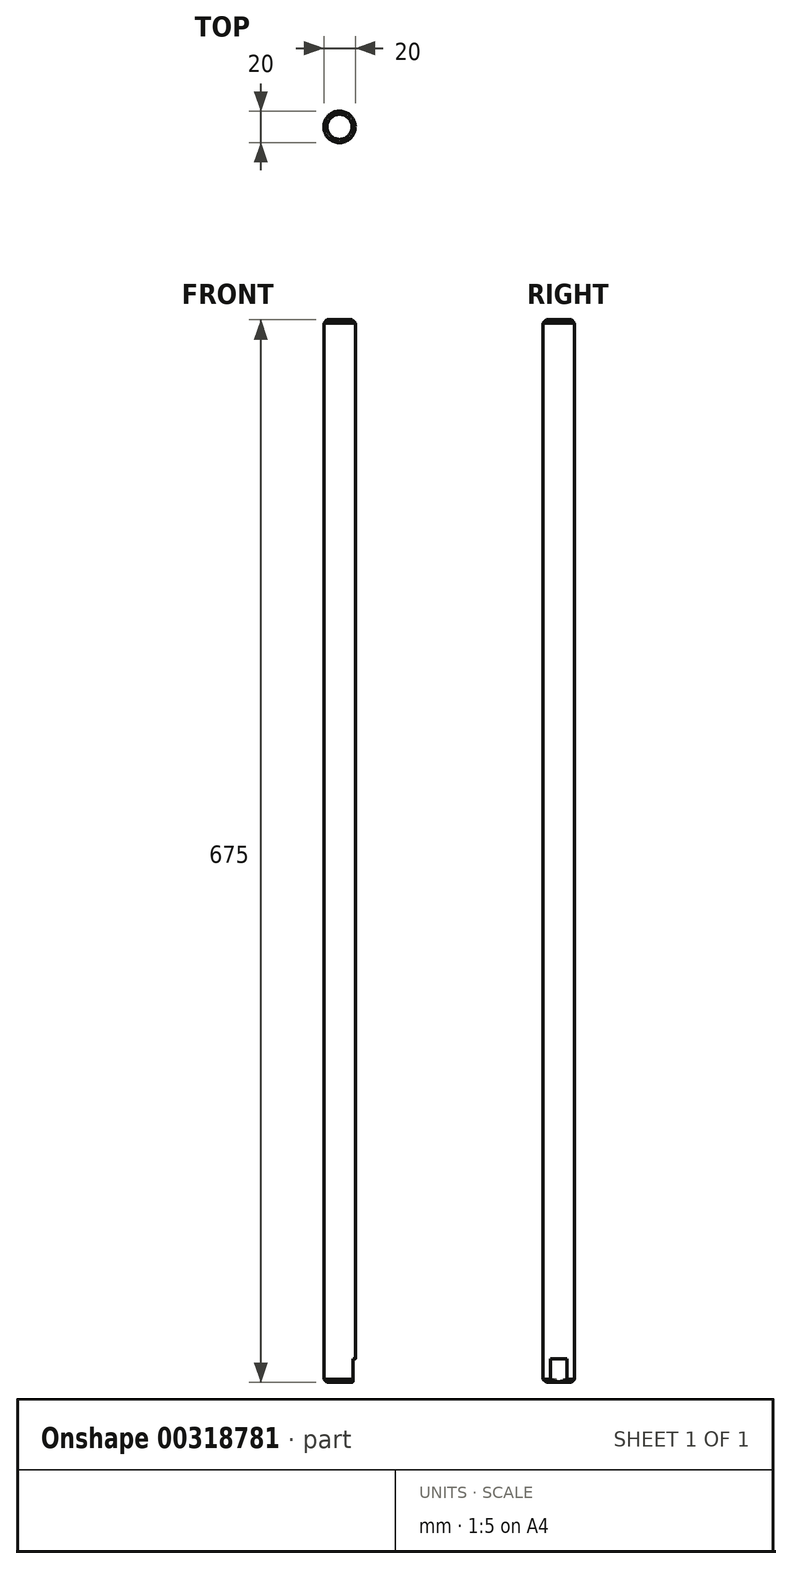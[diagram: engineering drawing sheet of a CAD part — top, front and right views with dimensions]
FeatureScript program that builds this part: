
annotation { "Feature Type Name" : "Feature", "Feature Type Description" : "" }
export const myFeature = defineFeature(function(context is Context, id is Id, definition is map)
    precondition{}
    {
        {
            var Q0;
            Q0=qCreatedBy(makeId("Top.planeOp"),FACE);
            var sketch = newSketch(context, id + "F0", { "sketchPlane" : qUnion([Q0])});
            skCircle(sketch, "E0", {"center": v(0, 0) * mm, "radius": 10 * mm});
            skSolve(sketch);
        }
        {
            var Q0;
            Q0=makeQuery(id+"F0.imprint","IMPRINT",FACE,{"disambiguationData":[TD([[makeQuery(id+"F0.imprint","IMPRINT",EDGE,{"derivedFrom":sQuery(id+"F0.wireOp",EDGE,"E0")}),1.0]])]});
            extrude(context, id + "F1", {"entities" : qUnion([Q0]), "offsetDistance" : 25 * mm, "depth" : 675 * mm});
        }
        {
            var Q0;
            Q0=makeQuery(id+"F1.opExtrude","CAP_EDGE",EDGE,{"disambiguationData":[OSD([sQuery(id+"F0.wireOp",EDGE,"E0")])],"isStart":true});
            var Q1;
            Q1=makeQuery(id+"F1.opExtrude","CAP_EDGE",EDGE,{"disambiguationData":[OSD([sQuery(id+"F0.wireOp",EDGE,"E0")])],"isStart":false});
            chamfer(context, id + "F2", {"entities" : qUnion([Q0, Q1]), "width" : 2 * mm, "tangentPropagation" : true});
        }
        {
            var Q0;
            Q0=qCreatedBy(makeId("Right.planeOp"),FACE);
            cPlane(context, id + "F3", {"entities" : qUnion([Q0]), "cplaneType" : CPlaneType.OFFSET, "offset" : 10 * mm, "width" : 150 * mm, "height" : 150 * mm});
        }
        {
            var Q0;
            Q0=qCreatedBy(id+"F3.planeOp",FACE);
            var sketch = newSketch(context, id + "F4", { "sketchPlane" : qUnion([Q0])});
            skLineSegment(sketch, "E1.bottom", {"start": v(10.5, 15) * mm, "end": v(-10.5, 15) * mm});
            skLineSegment(sketch, "E1.top", {"start": v(10.5, 0) * mm, "end": v(-10.5, 0) * mm});
            skLineSegment(sketch, "E1.left", {"start": v(10.5, 15) * mm, "end": v(10.5, 0) * mm});
            skLineSegment(sketch, "E1.right", {"start": v(-10.5, 15) * mm, "end": v(-10.5, 0) * mm});
            skPoint(sketch, "E1.middle", {"position": v(0, 7.5) * mm});
            skSolve(sketch);
        }
        {
            var Q0;
            Q0=makeQuery(id+"F4.imprint","IMPRINT",FACE,{"disambiguationData":[TD([[makeQuery(id+"F4.imprint","IMPRINT",EDGE,{"derivedFrom":sQuery(id+"F4.wireOp",EDGE,"E1.bottom")}),1.0]])]});
            extrude(context, id + "F5", {"entities" : qUnion([Q0]), "operationType" : NewBodyOperationType.REMOVE, "oppositeDirection" : true, "depth" : 1.5 * mm, "offsetDistance" : 25 * mm});
        }
    });
